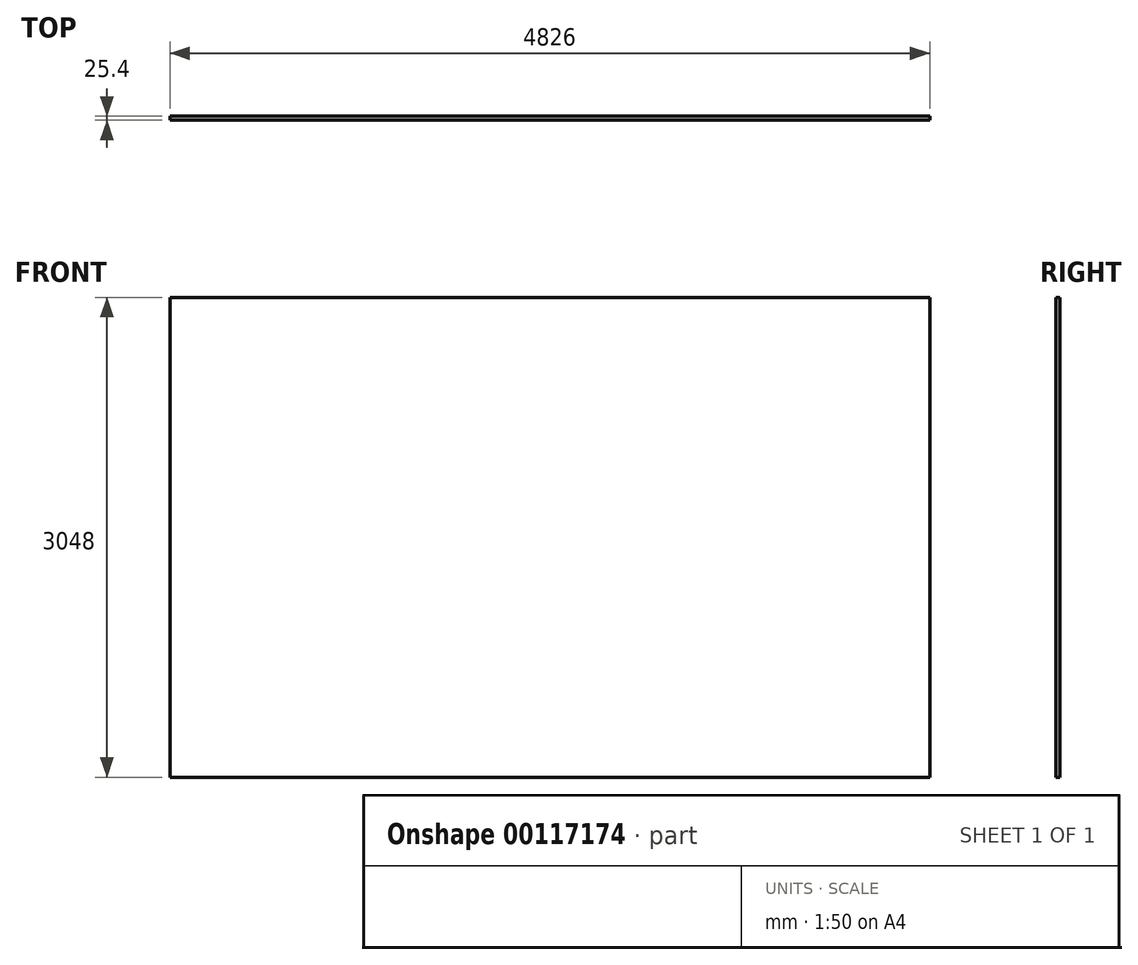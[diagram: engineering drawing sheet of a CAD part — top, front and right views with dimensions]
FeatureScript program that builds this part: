
annotation { "Feature Type Name" : "Feature", "Feature Type Description" : "" }
export const myFeature = defineFeature(function(context is Context, id is Id, definition is map)
    precondition{}
    {
        {
            var Q0;
            Q0=qCreatedBy(makeId("Front.planeOp"),FACE);
            var sketch = newSketch(context, id + "F0", { "sketchPlane" : qUnion([Q0])});
            skLineSegment(sketch, "E0.bottom", {"start": v(-1171.09, 2168.49) * mm, "end": v(3654.91, 2168.49) * mm});
            skLineSegment(sketch, "E0.top", {"start": v(-1171.09, -879.51) * mm, "end": v(3654.91, -879.51) * mm});
            skLineSegment(sketch, "E0.left", {"start": v(-1171.09, 2168.49) * mm, "end": v(-1171.09, -879.51) * mm});
            skLineSegment(sketch, "E0.right", {"start": v(3654.91, 2168.49) * mm, "end": v(3654.91, -879.51) * mm});
            skSolve(sketch);
        }
        {
            var Q0;
            Q0 = qSketchRegion(id + "F0", true);
            extrude(context, id + "F1", {"entities" : qUnion([Q0]), "depth" : 25.4 * mm});
        }
    });
